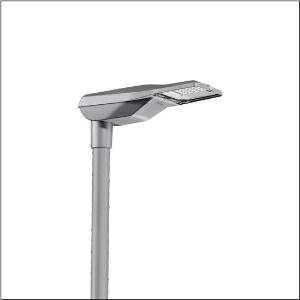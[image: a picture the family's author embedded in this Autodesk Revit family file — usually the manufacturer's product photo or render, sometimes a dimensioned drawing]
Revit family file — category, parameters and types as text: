
# Revit family: streetlight_sl_21_iq_micro___st1_0a_5xe1d21d08cb_1078
name_source: partatom
category: Lighting Fixtures
units: mm (PartAtom-declared; Revit-internal decimal feet)

## family parameters
Cut with Voids When Loaded = No
Host = Face
Light Source = No
Part Type = Normal
Room Calculation Point = No
Round Connector Dimension = Use Diameter
Shared = No

## types (1)
- --- (1 x LED, 2380 lm, 19.4 W, 2200K)
    Apparent Load = 19 VA
    CIE Flux Codes = 37 72 97 100 100
    Color Rendering = 70
    Color Temperature = 2200K
    Default Elevation = 1800 mm
    Description = Streetlight SL 21 iQ micro, mast luminaire, primary light control with lens, of PMMA, primary optical cover: cover, of toughened safety glass, transparent, light distribution: ST1.0a, light emission: direct distribution, primary light characteristic: asymmetric, installation type: post-top, side-entry, LED, High Power LED, rated luminous flux: 2.380lm, luminous efficacy: 123lm/W, light colour: 722, colour temperature: 2200K, control: Auto-Match, Temp-Guard, Lumen-Switch, Night-Set, Smart-Wire, Light-Fading, Desk-Remote (wireless, voltage-free reading and setting of iQ features in the workshop via application-optimized NFC function/RFID function), optimised constant luminous flux control (CLO 2.0), pre-setting: linear dimming characteristic, mains connection: 220..240V, AC, 50/60Hz, start of lifetime: 19W, end of service life: 20W, reduction: 10W, luminaire housing, of diecast aluminium, powder-coated, Siteco® metallic grey (DB 702S), corrosivity category C5 mid according to DIN EN ISO 12944, please order mast flange separately, inclination adjustable: 0°, 5°, 10°, 15°, sealing non-destructively replaceable, multi-level sealing system, length: 528mm, width: 235mm, height: 110mm, mast flange for spigot size: 42mm (side-entry): 5XC10008XM4, 60/48mm (side-entry/post-top): 5XC10108XM2, 76/60mm (side-entry/post-top): 5XC10108XM1, protection rating (complete): IP66, insulation class (complete): insulation class II (safety insulation), certification: CE, ENEC, ENEC+, VDE, impact resistance: IK09, permissible operating ambient temperature for outdoor applications: -40..+50°C, standard-compliant lighting for roads and squares, packaging unit: 1 piece

Light Distribution: ST1.0a
    Height = 110 mm
    Lamp = 1 x LED
    Lamp Light Flux = 2380 lm
    Lamp Power = 19.4 W
    Lamp count = 1
    Length = 528 mm
    Luminous efficacy = 123 lm/W
    Manufacturer = Siteco
    ModVariant = No
    Model = 5XE1D21D08CB
    Number of Poles = 1
    OnlyDefault = Yes
    Power Factor = 1
    Product Name = Streetlight SL 21 iQ micro | ST1.0a
    Product group = mast luminaire | pylon top
    ProductGroupID = 6100
    Protection Class = Protection class II
    Protection Degree = IP 66
    RLX_Detail_Level = 1
    RLX_Emergency_Light_Flux = 0 lm
    RLX_Emergency_Type = 0
    RLX_Emergency_Type_DB = No
    RlxData = <blob elided: 98629 chars, md5=df868d2a>
    Socket = socket
    Standby Power = 0 W
    System Light Flux = 2380 lm
    System Power = 19 W
    Type Comments = factory setting: luminous flux: 100 % | dim-lin: 254 | 387 mA
    Type Image = l_1006881.jpg
    URL = http://relux.com
    VarID = @adj_109163
    Voltage = 0 V
    Weight = 0.00 kg
    Width = 235 mm

## geometry (parser evidence)
native form markers: Blend x4, Sweep x9
no freeform markers — native parametric forms only
